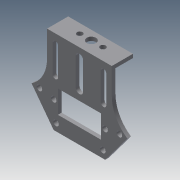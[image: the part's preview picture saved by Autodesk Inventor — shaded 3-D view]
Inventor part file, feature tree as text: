
AUTODESK INVENTOR PART (.ipt)
format: ipt  version: 2013 (Build 170138000, 138)  size: 993,792 bytes
history: native  units: mm
features: sketch x84, extrude x75, fillet x2
ambient origin geometry x8: Origin, YZ Plane, XZ Plane, XY Plane, X Axis, Y Axis, Z Axis, Center Point
bodies: Solid1 (feature_tree)
feature tree (161):
  extrude  "Extrusion1"  Depth=10.0mm
  extrude  "Extrusion2"  Depth=10.0mm
  sketch  "Sketch3"  dims[d8=2.0mm d9=0.0mm d11=3.0mm]
  extrude  "Extrusion3"  Depth=3.0mm
  extrude  "Extrusion4"  Depth=3.0mm
  extrude  "Extrusion5"  Depth=10.0mm TaperAngle=0.0deg
  extrude  "Extrusion6"  Depth=3.0mm
  sketch  "Sketch8"  dims[d24=10.0mm d25=0.0mm d26=2.0mm d27=0.0mm]
  extrude  "Extrusion7"  Depth=3.0mm
  extrude  "Extrusion8"  Depth=2.0mm TaperAngle=0.0deg
  extrude  "Extrusion9"  Depth=3.0mm
  extrude  "Extrusion10"  Depth=2.0mm TaperAngle=0.0deg
  extrude  "Extrusion11"  Depth=4.0mm
  extrude  "Extrusion12"  Depth=4.0mm
  extrude  "Extrusion13"  Depth=1.8mm
  sketch  "Sketch16"  dims[d61=4.0mm d62=4.0mm]
  extrude  "Extrusion14"  Depth=4.0mm
  extrude  "Extrusion15"  Depth=12.0mm
  extrude  "Extrusion16"  Depth=4.0mm
  extrude  "Extrusion17"  Depth=16.0mm
  sketch  "Sketch21"  dims[d75=30.0mm d77=2.0mm d78=0.0mm]
  extrude  "Extrusion18"  Depth=10.4mm
  extrude  "Extrusion19"  Depth=4.0mm
  extrude  "Extrusion20"  Depth=20.0mm
  extrude  "Extrusion21"  Depth=2.0mm TaperAngle=0.0deg
  extrude  "Extrusion22"  Depth=2.3mm
  extrude  "Extrusion23"  Depth=24.0mm
  extrude  "Extrusion24"  Depth=2.0mm TaperAngle=0.0deg
  extrude  "Extrusion25"  Depth=3.0mm
  extrude  "Extrusion26"  Depth=2.0mm TaperAngle=0.0deg
  extrude  "Extrusion27"  Depth=2.0mm TaperAngle=0.0deg
  extrude  "Extrusion28"  Depth=4.0mm
  extrude  "Extrusion29"  Depth=3.0mm
  extrude  "Extrusion30"  Depth=3.0mm
  extrude  "Extrusion31"  Depth=3.0mm
  extrude  "Extrusion32"  Depth=4.0mm
  extrude  "Extrusion33"  Depth=3.0mm
  extrude  "Extrusion34"  Depth=2.0mm TaperAngle=0.0deg
  extrude  "Extrusion35"  Depth=2.3mm
  extrude  "Extrusion36"  Depth=4.0mm
  extrude  "Extrusion37"  Depth=2.3mm
  sketch  "Sketch42"  dims[d147=24.0mm d148=24.0mm]
  sketch  "Sketch43"  dims[d149=2.0mm d150=0.0mm d151=2.0mm d152=0.0mm]
  extrude  "Extrusion38"  Depth=2.0mm TaperAngle=0.0deg
  extrude  "Extrusion39"  Depth=2.0mm TaperAngle=0.0deg
  extrude  "Extrusion40"  Depth=20.0mm
  extrude  "Extrusion41"  Depth=20.0mm
  extrude  "Extrusion42"  Depth=24.0mm
  extrude  "Extrusion43"  Depth=2.0mm TaperAngle=0.0deg
  extrude  "Extrusion44"  Depth=3.0mm
  extrude  "Extrusion45"  Depth=20.0mm
  extrude  "Extrusion46"  Depth=2.0mm TaperAngle=0.0deg
  extrude  "Extrusion47"  Depth=3.0mm
  extrude  "Extrusion48"  Depth=3.0mm
  fillet  "Fillet1"  Radius=3.0mm
  extrude  "Extrusion49"  Depth=2.5mm
  fillet  "Fillet2"  Radius=2.0mm
  extrude  "Extrusion50"  Depth=12.5mm
  extrude  "Extrusion51"  Depth=2.5mm
  extrude  "Extrusion52"  Depth=20.0mm
  extrude  "Extrusion53"  Depth=25.0mm
  extrude  "Extrusion54"  Depth=2.0mm TaperAngle=0.0deg
  extrude  "Extrusion55"  Depth=1.5mm
  extrude  "Extrusion56"  Depth=20.0mm
  extrude  "Extrusion57"  Depth=20.0mm
  extrude  "Extrusion58"  Depth=24.0mm
  extrude  "Extrusion59"  Depth=3.4mm
  extrude  "Extrusion60"  Depth=3.0mm
  extrude  "Extrusion61"  Depth=3.0mm
  extrude  "Extrusion62"  Depth=2.0mm TaperAngle=0.0deg
  sketch  "Sketch67"  dims[d218=3.0mm d219=3.0mm]
  extrude  "Extrusion63"  Depth=17.0mm
  extrude  "Extrusion64"  Depth=2.0mm TaperAngle=0.0deg
  extrude  "Extrusion65"  Depth=14.4mm
  sketch  "Sketch71"  dims[d228=1.5mm d229=3.0mm]
  sketch  "Sketch72"  dims[d230=2.0mm d231=0.0mm d233=2.0mm d234=0.0mm]
  extrude  "Extrusion66"  Depth=1.5mm
  sketch  "Sketch73"  dims[d236=14.5mm d237=13.95mm]
  sketch  "Sketch74"  dims[d238=13.95mm d239=3.0mm]
  extrude  "Extrusion67"  Depth=3.0mm
  extrude  "Extrusion68"  Depth=2.0mm TaperAngle=0.0deg
  extrude  "Extrusion69"  Depth=1.5mm
  extrude  "Extrusion70"  Depth=14.4mm
  extrude  "Extrusion71"  Depth=3.0mm
  extrude  "Extrusion72"  Depth=2.0mm TaperAngle=0.0deg
  extrude  "Extrusion73"  Depth=13.95mm
  sketch  "Sketch82"  dims[d253=4.0mm]
  extrude  "Extrusion74"  Depth=3.0mm
  extrude  "Extrusion75"  Depth=2.0mm TaperAngle=0.0deg
  sketch  "Sketch1"  dims[d2=10.0mm d3=10.0mm]
  sketch  "Sketch2"  dims[d4=10.0mm d7=10.0mm]
  sketch  "Sketch4"  dims[d12=3.0mm d14=3.0mm]
  sketch  "Sketch5"  dims[d15=3.0mm d16=10.0mm d17=0.0mm]
  sketch  "Sketch6"  dims[d20=6.0mm d21=3.0mm]
  sketch  "Sketch7"  dims[d22=6.0mm d23=3.0mm]
  sketch  "Sketch9"  dims[d34=3.0mm d36=3.0mm]
  sketch  "Sketch10"  dims[d37=2.0mm d38=0.0mm d39=2.0mm d40=0.0mm]
  sketch  "Sketch11"  dims[d48=2.0mm d49=4.0mm]
  sketch  "Sketch12"  dims[d51=12.0mm d52=4.0mm]
  sketch  "Sketch13"  dims[d53=2.0mm d54=0.0mm d55=1.8mm]
  sketch  "Sketch14"  dims[d56=2.0mm d57=4.0mm]
  sketch  "Sketch15"  dims[d58=2.0mm d59=0.0mm d60=12.0mm]
  sketch  "Sketch17"  dims[d63=2.0mm d64=0.0mm d65=16.0mm]
  sketch  "Sketch18"  dims[d66=12.0mm d67=10.4mm]
  sketch  "Sketch19"  dims[d68=2.0mm d69=0.0mm d70=4.0mm]
  sketch  "Sketch20"  dims[d71=2.0mm d72=0.0mm d74=20.0mm]
  sketch  "Sketch22"  dims[d83=2.3mm d84=2.3mm]
  sketch  "Sketch23"  dims[d85=2.0mm d86=0.0mm d90=24.0mm]
  sketch  "Sketch24"  dims[d92=24.0mm d93=2.0mm d94=0.0mm]
  sketch  "Sketch25"  dims[d97=3.0mm d98=3.0mm]
  sketch  "Sketch26"  dims[d100=3.0mm d101=2.0mm d102=0.0mm]
  sketch  "Sketch27"  dims[d103=2.0mm d104=0.0mm d105=2.0mm d106=0.0mm]
  sketch  "Sketch28"  dims[d111=4.0mm d112=4.0mm]
  sketch  "Sketch29"  dims[d113=3.0mm d114=3.0mm]
  sketch  "Sketch30"  dims[d116=3.0mm d117=3.0mm]
  sketch  "Sketch31"  dims[d118=3.0mm d119=3.0mm]
  sketch  "Sketch32"  dims[d120=3.0mm d121=4.0mm]
  sketch  "Sketch33"  dims[d122=3.0mm d123=3.0mm]
  sketch  "Sketch34"  dims[d124=3.0mm d125=2.0mm d126=0.0mm]
  sketch  "Sketch35"  dims[d127=2.3mm d128=2.3mm]
  sketch  "Sketch36"  dims[d131=4.0mm d132=4.0mm]
  sketch  "Sketch37"  dims[d133=2.0mm d134=0.0mm d135=2.3mm]
  sketch  "Sketch38"  dims[d136=2.3mm d137=2.0mm d138=0.0mm]
  sketch  "Sketch39"  dims[d139=3.0mm d140=2.0mm d141=0.0mm]
  sketch  "Sketch40"  dims[d142=2.0mm d143=0.0mm d144=20.0mm]
  sketch  "Sketch41"  dims[d145=14.0mm d146=20.0mm]
  sketch  "Sketch44"  dims[d157=3.0mm d158=3.0mm]
  sketch  "Sketch45"  dims[d159=2.0mm d160=0.0mm d161=20.0mm]
  sketch  "Sketch46"  dims[d162=20.0mm d163=2.0mm d164=0.0mm]
  sketch  "Sketch47"  dims[d165=2.0mm d166=0.0mm d167=3.0mm]
  sketch  "Sketch48"  dims[d168=3.0mm d169=3.0mm d170=3.0mm]
  sketch  "Sketch49"  dims[d171=2.5mm d172=2.5mm d173=2.0mm d174=0.0mm]
  sketch  "Sketch50"  dims[d175=2.0mm d176=0.0mm d178=12.5mm]
  sketch  "Sketch51"  dims[d179=12.5mm d180=2.5mm]
  sketch  "Sketch52"  dims[d181=2.5mm d183=20.0mm]
  sketch  "Sketch53"  dims[d185=20.0mm d186=25.0mm]
  sketch  "Sketch54"  dims[d187=25.0mm d188=2.0mm d189=0.0mm]
  sketch  "Sketch55"  dims[d190=1.5mm d191=1.5mm]
  sketch  "Sketch56"  dims[d192=1.5mm d193=20.0mm]
  sketch  "Sketch57"  dims[d194=1.5mm d195=20.0mm]
  sketch  "Sketch58"  dims[d196=24.0mm d197=24.0mm]
  sketch  "Sketch59"  dims[d198=2.0mm d199=0.0mm d200=3.4mm]
  sketch  "Sketch60"  dims[d201=3.4mm d202=3.0mm]
  sketch  "Sketch61"  dims[d203=3.0mm d204=3.0mm]
  sketch  "Sketch62"  dims[d205=3.0mm d206=2.0mm d207=0.0mm]
  sketch  "Sketch63"  dims[d208=2.0mm d209=0.0mm d210=17.0mm]
  sketch  "Sketch64"  dims[d211=14.4mm d212=2.0mm d213=0.0mm]
  sketch  "Sketch65"  dims[d214=19.5mm d215=14.4mm]
  sketch  "Sketch66"  dims[d216=1.5mm d217=1.5mm]
  sketch  "Sketch68"  dims[d220=2.0mm d221=0.0mm d222=2.0mm d223=0.0mm]
  sketch  "Sketch69"  dims[d224=19.5mm d225=1.5mm]
  sketch  "Sketch70"  dims[d226=3.0mm d227=14.4mm]
  sketch  "Sketch75"  dims[d241=3.0mm d242=2.0mm d243=0.0mm]
  sketch  "Sketch76"  dims[d244=2.0mm d245=0.0mm]
  sketch  "Sketch77"  dims[d248=14.4mm]
  sketch  "Sketch78"  dims[d249=21.6mm]
  sketch  "Sketch79"  dims[d250=2.0mm]
  sketch  "Sketch80"  dims[d251=2.0mm]
  sketch  "Sketch81"  dims[d252=4.0mm]
  sketch  "Sketch83"  dims[d254=2.0mm d255=0.0mm]
  sketch  "Sketch84"  dims[d256=19.0mm d259=19.0mm d260=2.0mm d261=0.0mm d262=10.0mm d263=4.0mm d264=4.0mm d265=2.0mm d266=0.0mm d267=2.0mm d268=0.0mm d269=2.0mm d270=0.0mm d271=2.0mm d272=0.0mm d273=3.6mm d274=2.0mm d275=0.0mm d276=1.5mm d277=10.0mm d278=0.0mm d279=2.0mm d280=0.5mm d281=0.0mm d282=0.5mm d283=1.5mm d284=0.0mm d285=1.5mm d286=0.0mm d287=10.4mm d288=14.398895mm d289=16.0mm d290=1.5mm d291=0.0mm d292=1.5mm d293=0.0mm d294=10.0mm d295=0.0mm d296=10.0mm d297=0.0mm d298=10.0mm d299=0.0mm d300=20.0mm d301=0.0mm d306=1.5mm d307=0.0mm d308=4.0mm d309=7.0mm d310=16.0mm d311=3.0mm d312=7.0mm d313=16.0mm d314=1.5mm d315=0.0mm d316=5.0mm d317=1.5mm d318=0.0mm d319=1.5mm d320=10.0mm d321=0.0mm d322=7.0mm d323=7.0mm d324=4.0mm d325=7.0mm d326=4.0mm d327=7.0mm d328=4.0mm d329=1.5mm d330=0.0mm d331=4.0mm d332=4.129mm d333=7.0mm d335=3.072mm d336=7.0mm d337=15.0mm d338=1.5mm d339=0.0mm d341=1.5mm d342=0.0mm d343=0.5mm d344=7.0mm d345=18.0mm d346=7.0mm d347=1.5mm d348=0.0mm d349=7.0mm d351=7.0mm d353=1.5mm d354=0.0mm d359=8.3mm d360=11.6mm d361=23.6mm d362=12.4mm d363=1.5mm d364=0.0mm d365=27.9mm d366=0.4mm d367=1.5mm d368=0.0mm d370=0.3mm d371=0.3mm d372=1.5mm d373=0.0mm d374=5.0mm d375=5.0mm d376=1.5mm d377=0.0mm d378=6.3mm d379=12.6mm d380=3.0mm d381=3.0mm d382=1.5mm d383=0.0mm d384=2.0mm d385=0.0mm d386=0.5mm d387=0.0mm d388=0.5mm d389=0.0mm d390=3.0mm d391=4.5mm d392=3.0mm d393=4.5mm d394=3.0mm d395=3.0mm d396=4.0mm d397=3.0mm d398=15.0mm d399=15.0mm d400=15.0mm d401=4.0mm d402=3.0mm d403=3.0mm d404=2.0mm d405=0.0mm]
